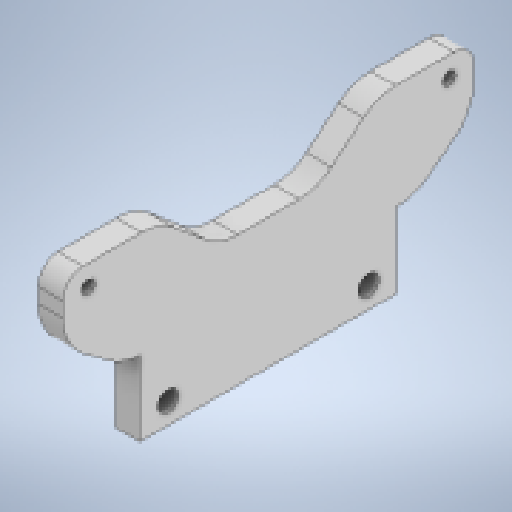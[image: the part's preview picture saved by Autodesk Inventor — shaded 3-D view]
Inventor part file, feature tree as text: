
AUTODESK INVENTOR PART (.ipt)
format: ipt  version: 2024.2 (Build 282272000, 272)  size: 279,552 bytes
history: native  units: in
note: dims shown in document units (in); Inventor stores cm internally (conversion verified against a paired STEP export)
features: extrude x6, sketch x6, projected_geometry x5, other x2, fillet x1, reference x1
ambient origin geometry x8: Origin, YZ Plane, XZ Plane, XY Plane, X Axis, Y Axis, Z Axis, Center Point
bodies: Solid1 (feature_tree)
feature tree (21):
  extrude  "Extrusion1"  Depth=3.2283in
  extrude  "Extrusion2"  Depth=0.0787in
  extrude  "Extrusion3"  Depth=0.0787in TaperAngle=0.0deg
  extrude  "Extrusion4"  Depth=0.1811in
  extrude  "Extrusion5"  Depth=0.1024in
  extrude  "Extrusion6"  TaperAngle=0.0deg  [1 undecoded]
  fillet  "Fillet1"  Radius=0.1614in
  sketch  "Sketch1"  dims[d0=3.2283in d1=3.2283in]
  sketch  "Sketch2"  dims[d2=0.0787in d3=0.0in d4=0.5906in]
  reference  "Reference1"
  sketch  "Sketch3"  dims[d5=0.0787in d6=0.0in d7=0.5906in d8=0.0in]
  projected_geometry  "Projected Loop1"
  projected_geometry  "Projected Loop2"
  sketch  "Sketch4"  dims[d9=0.1811in d10=0.1811in]
  projected_geometry  "Projected Loop3"
  sketch  "Sketch5"  dims[d11=0.0551in d12=0.0in d13=0.1024in]
  projected_geometry  "Projected Loop4"
  sketch  "Sketch6"  dims[d14=0.1024in d15=0.0in d16=0.0in d17=0.1614in d18=0.1614in d19=0.1654in d20=1.5748in d21=0.3937in d22=0.0in d29=0.0787in]
  projected_geometry  "Projected Loop5"
  other  "4_Camera.iam"
  other  "Astra plus Camera:1"
note: 1 required parameter value undecoded (feature->parameter linkage not recoverable at this tier; creation-order binding heuristic only, values carry confidence <= 0.55)
